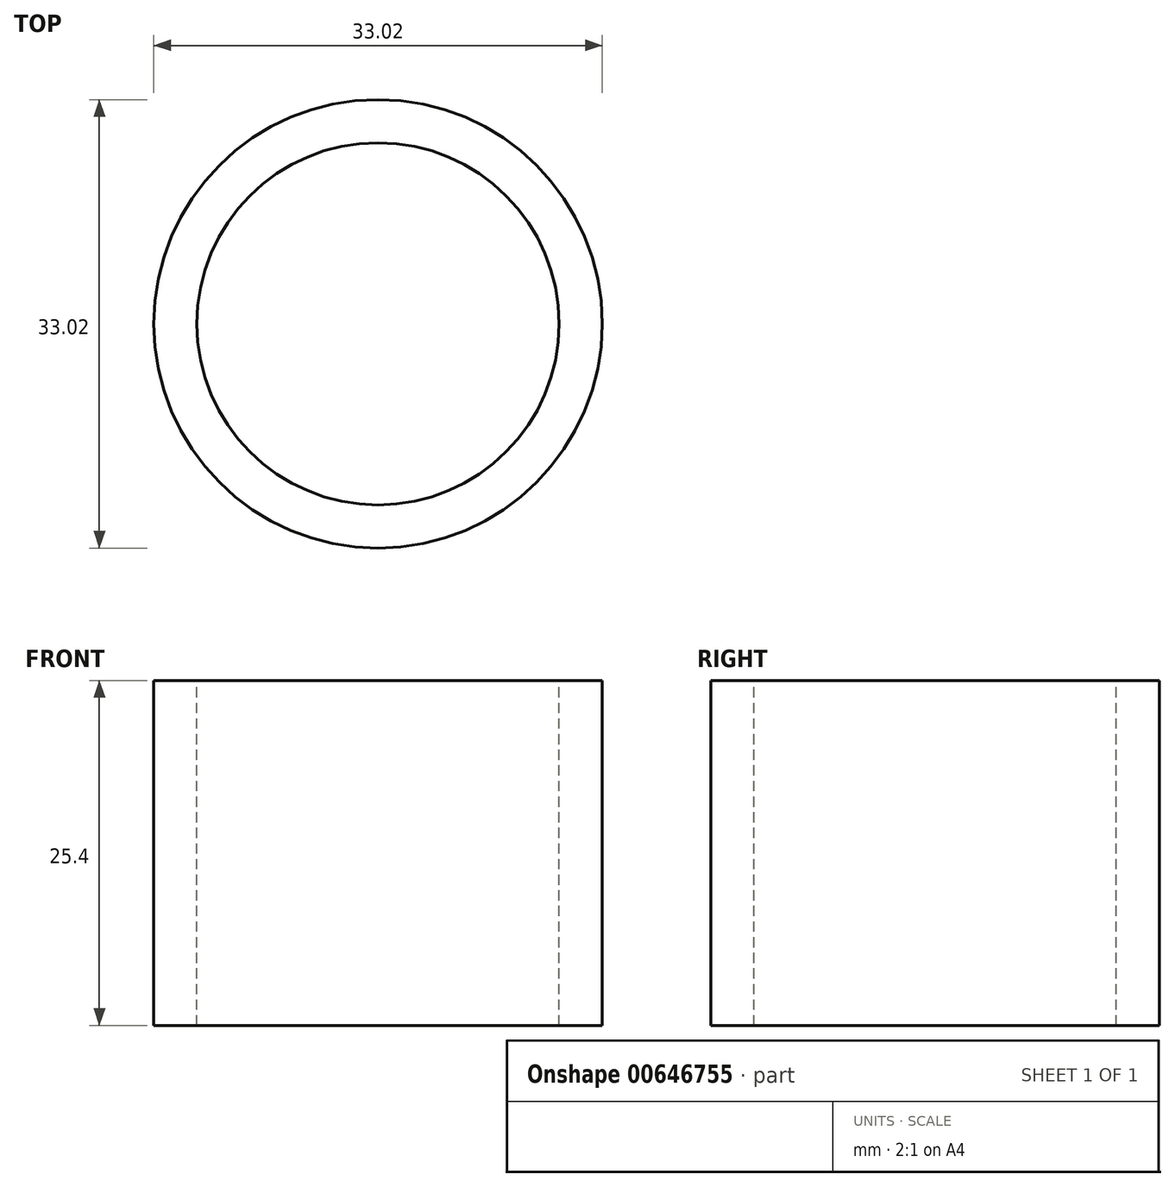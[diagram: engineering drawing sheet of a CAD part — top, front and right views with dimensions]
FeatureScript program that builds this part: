
annotation { "Feature Type Name" : "Feature", "Feature Type Description" : "" }
export const myFeature = defineFeature(function(context is Context, id is Id, definition is map)
    precondition{}
    {
        {
            var Q0;
            Q0=qCreatedBy(makeId("Top.planeOp"),FACE);
            var sketch = newSketch(context, id + "F0", { "sketchPlane" : qUnion([Q0])});
            skCircle(sketch, "E0", {"center": v(0, 0) * mm, "radius": 13.34 * mm});
            skCircle(sketch, "E1", {"center": v(0, 0) * mm, "radius": 16.51 * mm});
            skSolve(sketch);
        }
        {
            var Q0;
            Q0=sQuery(id+"F0.wireOp",EDGE,"E1");
            var Q1;
            Q1=sQuery(id+"F0.wireOp",EDGE,"E0");
            extrude(context, id + "F1", {"bodyType" : ToolBodyType.SURFACE, "surfaceEntities" : qUnion([Q0, Q1]), "depth" : 25.4 * mm, "offsetDistance" : 25.4 * mm});
        }
    });
